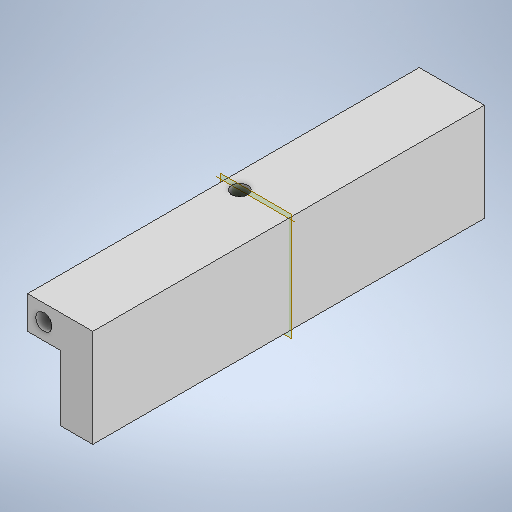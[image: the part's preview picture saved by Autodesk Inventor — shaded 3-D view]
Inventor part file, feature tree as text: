
AUTODESK INVENTOR PART (.ipt)
format: ipt  version: 2025.2 (Build 292293000, 293)  size: 223,232 bytes
history: native  units: in
note: dims shown in document units (in); Inventor stores cm internally (conversion verified against a paired STEP export)
features: extrude x3, sketch x3, plane x1, mirror x1, other x1
ambient origin geometry x8: Origin, YZ Plane, XZ Plane, XY Plane, X Axis, Y Axis, Z Axis, Center Point
bodies: Solid1 (feature_tree)
feature tree (9):
  extrude  "Extrusion1"  Depth=0.5in
  extrude  "Extrusion2"  Depth=0.5in
  extrude  "Extrusion3"  Depth=2.0in
  plane  "Work Plane1"
  mirror  "Mirror1"
  sketch  "Sketch1"  dims[d0=1.0in d1=0.5in]
  sketch  "Sketch2"  dims[d2=0.5in d3=0.5in]
  sketch  "Sketch3"  dims[d4=6.0in d5=0.0in d6=0.25in d7=3.0in d8=0.25in d9=0.5in d10=0.0in d11=0.25in d12=0.25in d13=0.25in d14=2.0in d15=0.0in d16=90.0deg]
  other  "Work Axis1"
